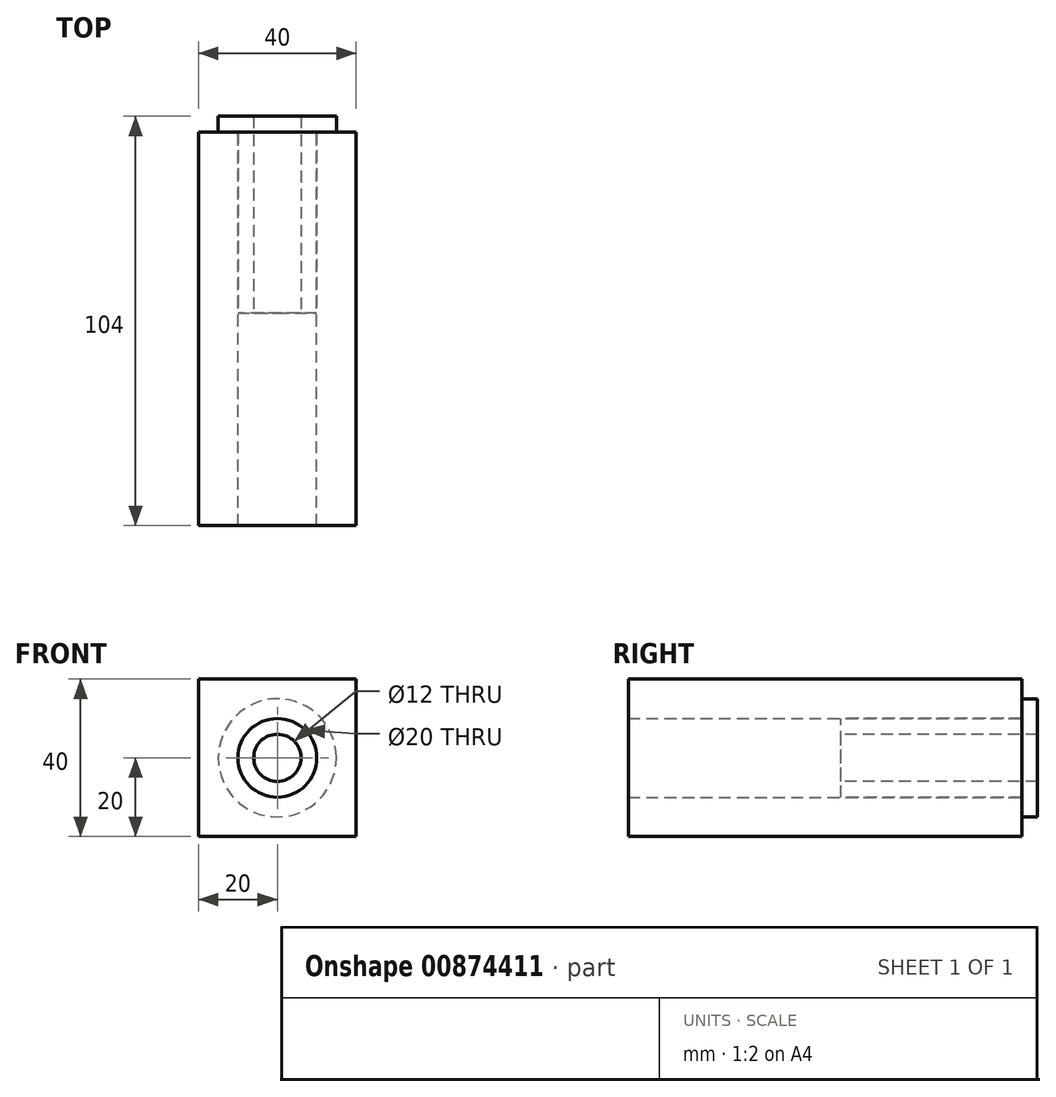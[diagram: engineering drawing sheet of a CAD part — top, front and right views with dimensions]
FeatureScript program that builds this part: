
annotation { "Feature Type Name" : "Feature", "Feature Type Description" : "" }
export const myFeature = defineFeature(function(context is Context, id is Id, definition is map)
    precondition{}
    {
        {
            var Q0;
            Q0=qCreatedBy(makeId("Front.planeOp"),FACE);
            var sketch = newSketch(context, id + "F0", { "sketchPlane" : qUnion([Q0])});
            skLineSegment(sketch, "E0.bottom", {"start": v(-20, 20) * mm, "end": v(20, 20) * mm});
            skLineSegment(sketch, "E0.top", {"start": v(-20, -20) * mm, "end": v(20, -20) * mm});
            skLineSegment(sketch, "E0.left", {"start": v(-20, 20) * mm, "end": v(-20, -20) * mm});
            skLineSegment(sketch, "E0.right", {"start": v(20, 20) * mm, "end": v(20, -20) * mm});
            skLineSegment(sketch, "E1", {"start": v(0, 0) * mm, "end": v(0, 20) * mm, "construction": true});
            skLineSegment(sketch, "E2", {"start": v(0, 0) * mm, "end": v(-20, 0) * mm, "construction": true});
            skCircle(sketch, "E3", {"center": v(0, 0) * mm, "radius": 10 * mm});
            skSolve(sketch);
        }
        {
            var Q0;
            Q0=makeQuery(id+"F0.imprint","IMPRINT",FACE,{"disambiguationData":[TD([[makeQuery(id+"F0.imprint","IMPRINT",EDGE,{"derivedFrom":sQuery(id+"F0.wireOp",EDGE,"E0.bottom")}),-1.0]])]});
            extrude(context, id + "F1", {"entities" : qUnion([Q0]), "depth" : 100 * mm, "offsetDistance" : 25 * mm});
        }
        {
            var Q0;
            Q0=qCreatedBy(makeId("Right.planeOp"),FACE);
            var sketch = newSketch(context, id + "F2", { "sketchPlane" : qUnion([Q0])});
            skLineSegment(sketch, "E4", {"start": v(-46, 10) * mm, "end": v(0, 10) * mm});
            skLineSegment(sketch, "E5", {"start": v(0, 10) * mm, "end": v(0, 15) * mm});
            skLineSegment(sketch, "E6", {"start": v(0, 15) * mm, "end": v(4, 15) * mm});
            skLineSegment(sketch, "E7", {"start": v(-46, 6) * mm, "end": v(-46, 10) * mm});
            skLineSegment(sketch, "E8", {"start": v(-46, 6) * mm, "end": v(4, 6) * mm});
            skLineSegment(sketch, "E9", {"start": v(4, 6) * mm, "end": v(4, 15) * mm});
            skLineSegment(sketch, "E10", {"start": v(-46, 0) * mm, "end": v(0, 0) * mm, "construction": true});
            skSolve(sketch);
        }
        {
            var Q0;
            Q0=makeQuery(id+"F2.imprint","IMPRINT",FACE,{"disambiguationData":[TD([[makeQuery(id+"F2.imprint","IMPRINT",EDGE,{"derivedFrom":sQuery(id+"F2.wireOp",EDGE,"E4")}),-1.0]])]});
            var Q1;
            Q1=sQuery(id+"F2.wireOp",EDGE,"E10");
            revolve(context, id + "F3", {"surfaceOperationType" : NewSurfaceOperationType.NEW, "entities" : qUnion([Q0]), "axis" : qUnion([Q1]), "revolveType" : RevolveType.FULL});
        }
    });
